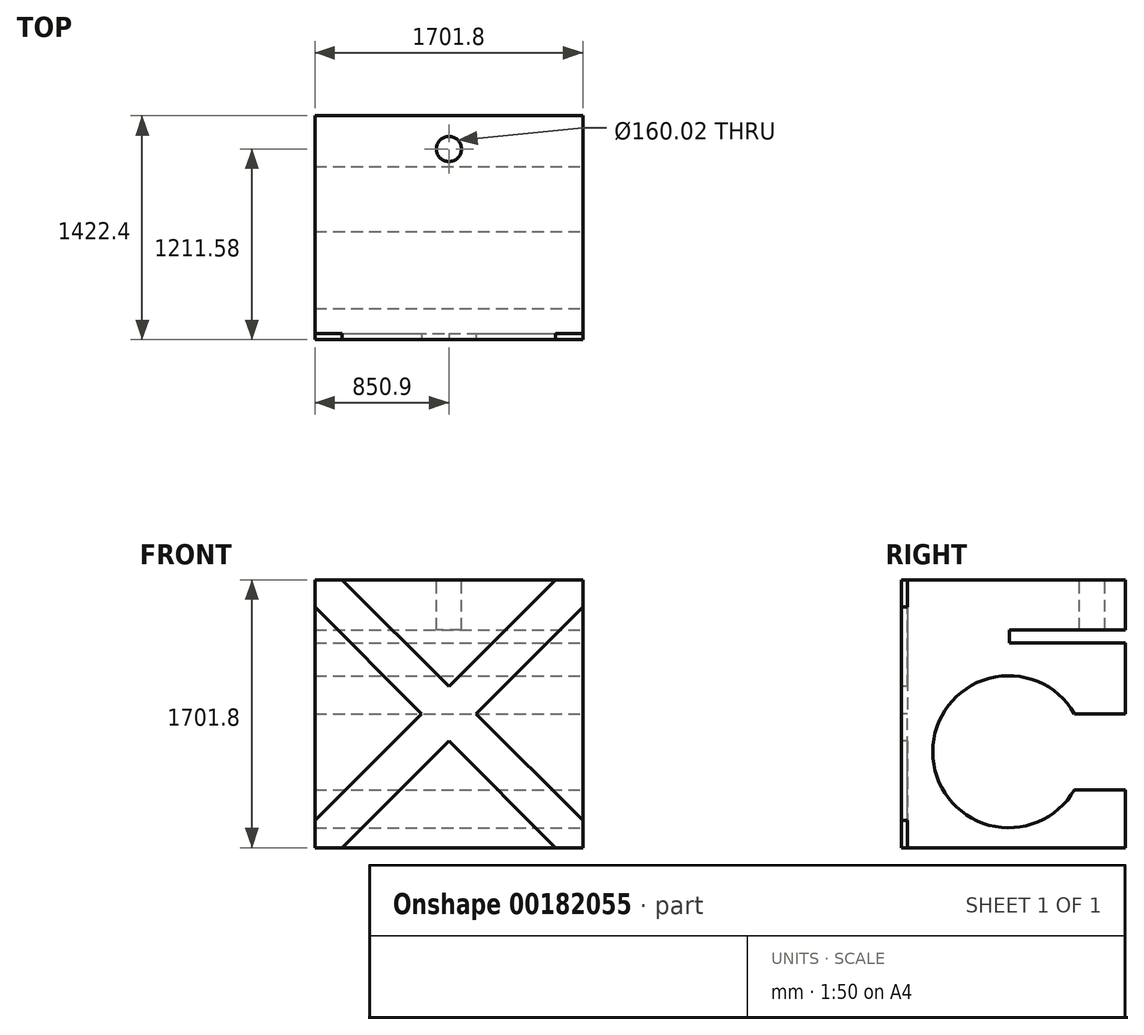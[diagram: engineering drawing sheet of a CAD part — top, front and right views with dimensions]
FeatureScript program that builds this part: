
annotation { "Feature Type Name" : "Feature", "Feature Type Description" : "" }
export const myFeature = defineFeature(function(context is Context, id is Id, definition is map)
    precondition{}
    {
        {
            var Q0;
            Q0=qCreatedBy(makeId("Front.planeOp"),FACE);
            var sketch = newSketch(context, id + "F0", { "sketchPlane" : qUnion([Q0])});
            skLineSegment(sketch, "E0.bottom", {"start": v(850.9, 850.9) * mm, "end": v(-850.9, 850.9) * mm});
            skLineSegment(sketch, "E0.top", {"start": v(850.9, -850.9) * mm, "end": v(-850.9, -850.9) * mm});
            skLineSegment(sketch, "E0.left", {"start": v(850.9, 850.9) * mm, "end": v(850.9, -850.9) * mm});
            skLineSegment(sketch, "E0.right", {"start": v(-850.9, 850.9) * mm, "end": v(-850.9, -850.9) * mm});
            skPoint(sketch, "E0.middle", {"position": v(0, 0) * mm});
            skSolve(sketch);
        }
        {
            var Q0;
            Q0 = qSketchRegion(id + "F0", true);
            extrude(context, id + "F1", {"entities" : qUnion([Q0]), "depth" : 1422.4 * mm});
        }
        {
            var Q0;
            Q0=makeQuery(id+"F1.opExtrude","CAP_FACE",FACE,{"disambiguationData":[OSD([sQuery(id+"F0.wireOp",EDGE,"E0.bottom"),sQuery(id+"F0.wireOp",EDGE,"E0.top"),sQuery(id+"F0.wireOp",EDGE,"E0.left"),sQuery(id+"F0.wireOp",EDGE,"E0.right")])],"isStart":false});
            var sketch = newSketch(context, id + "F2", { "sketchPlane" : qUnion([Q0])});
            skLineSegment(sketch, "E1", {"start": v(-980.53, -808.1) * mm, "end": v(797.03, 969.45) * mm});
            skLineSegment(sketch, "E2", {"start": v(-980.53, -808.1) * mm, "end": v(-808.1, -980.53) * mm});
            skLineSegment(sketch, "E3", {"start": v(-808.1, -980.53) * mm, "end": v(969.45, 797.03) * mm});
            skLineSegment(sketch, "E4", {"start": v(797.03, 969.45) * mm, "end": v(969.45, 797.03) * mm});
            skLineSegment(sketch, "E5", {"start": v(-1008.5, 836.08) * mm, "end": v(787.55, -959.97) * mm});
            skLineSegment(sketch, "E6", {"start": v(-836.08, 1008.5) * mm, "end": v(959.97, -787.55) * mm});
            skLineSegment(sketch, "E7", {"start": v(787.55, -959.97) * mm, "end": v(959.97, -787.55) * mm});
            skLineSegment(sketch, "E8", {"start": v(-1008.5, 836.08) * mm, "end": v(-836.08, 1008.5) * mm});
            skSolve(sketch);
        }
        {
            var Q0;
            {var subQ5=sQuery(id+"F2.wireOp",EDGE,"E5");var subQ6=sQuery(id+"F2.wireOp",EDGE,"E1");var subQ7=makeQuery(id+"F2.imprint","INTERSECT",VERTEX,{"derivedFrom":[subQ6,subQ5]});Q0=makeQuery(id+"F2.imprint","IMPRINT",FACE,{"disambiguationData":[TD([[makeQuery(id+"F2.imprint","IMPRINT",EDGE,{"disambiguationData":[TD([[subQ7,-1.0]])],"derivedFrom":subQ6}),1.0]])]});}
            var Q1;
            {var subQ5=sQuery(id+"F2.wireOp",EDGE,"E5");var subQ6=sQuery(id+"F2.wireOp",EDGE,"E1");var subQ7=makeQuery(id+"F2.imprint","INTERSECT",VERTEX,{"derivedFrom":[subQ6,subQ5]});Q1=makeQuery(id+"F2.imprint","IMPRINT",FACE,{"disambiguationData":[TD([[makeQuery(id+"F2.imprint","IMPRINT",EDGE,{"disambiguationData":[TD([[subQ7,1.0]])],"derivedFrom":subQ6}),-1.0]])]});}
            var Q2;
            {var subQ0=sQuery(id+"F2.wireOp",EDGE,"E5");var subQ1=sQuery(id+"F2.wireOp",EDGE,"E1");var subQ2=makeQuery(id+"F2.imprint","INTERSECT",VERTEX,{"derivedFrom":[subQ1,subQ0]});Q2=makeQuery(id+"F2.imprint","IMPRINT",FACE,{"disambiguationData":[TD([[makeQuery(id+"F2.imprint","IMPRINT",EDGE,{"disambiguationData":[TD([[subQ2,-1.0]])],"derivedFrom":subQ1}),-1.0]])]});}
            var Q3;
            {var subQ0=sQuery(id+"F2.wireOp",EDGE,"E6");var subQ1=sQuery(id+"F2.wireOp",EDGE,"E1");var subQ2=makeQuery(id+"F2.imprint","INTERSECT",VERTEX,{"derivedFrom":[subQ1,subQ0]});Q3=makeQuery(id+"F2.imprint","IMPRINT",FACE,{"disambiguationData":[TD([[makeQuery(id+"F2.imprint","IMPRINT",EDGE,{"disambiguationData":[TD([[subQ2,-1.0]])],"derivedFrom":subQ1}),-1.0]])]});}
            var Q4;
            {var subQ3=sQuery(id+"F2.wireOp",EDGE,"E5");var subQ6=sQuery(id+"F2.wireOp",EDGE,"E3");var subQ9=makeQuery(id+"F2.imprint","INTERSECT",VERTEX,{"derivedFrom":[subQ6,subQ3]});Q4=makeQuery(id+"F2.imprint","IMPRINT",FACE,{"disambiguationData":[TD([[makeQuery(id+"F2.imprint","IMPRINT",EDGE,{"disambiguationData":[TD([[subQ9,-1.0]])],"derivedFrom":subQ6}),-1.0]])]});}
            var Q5;
            Q5=sQuery(id+"F2.wireOp",EDGE,"E2");
            var Q6;
            Q6=sQuery(id+"F2.wireOp",EDGE,"E3");
            var Q7;
            Q7=sQuery(id+"F2.wireOp",EDGE,"E4");
            var Q8;
            Q8=sQuery(id+"F2.wireOp",EDGE,"E1");
            var Q9;
            Q9=sQuery(id+"F2.wireOp",EDGE,"E5");
            var Q10;
            Q10=sQuery(id+"F2.wireOp",EDGE,"E7");
            var Q11;
            Q11=sQuery(id+"F2.wireOp",EDGE,"E8");
            var Q12;
            Q12=sQuery(id+"F2.wireOp",EDGE,"E6");
            extrude(context, id + "F3", {"entities" : qUnion([Q0, Q1, Q2, Q3, Q4]), "operationType" : NewBodyOperationType.REMOVE, "surfaceEntities" : qUnion([Q5, Q6, Q7, Q8, Q9, Q10, Q11, Q12]), "oppositeDirection" : true, "depth" : 38.1 * mm});
        }
        {
            var Q0;
            Q0=makeQuery(id+"F1.opExtrude","SWEPT_FACE",FACE,{"disambiguationData":[OSD([sQuery(id+"F0.wireOp",EDGE,"E0.left")])]});
            var sketch = newSketch(context, id + "F4", { "sketchPlane" : qUnion([Q0])});
            skLineSegment(sketch, "E9", {"start": v(0, 533.4) * mm, "end": v(-736.6, 533.4) * mm});
            skLineSegment(sketch, "E10", {"start": v(-736.6, 533.4) * mm, "end": v(-736.6, 449.58) * mm});
            skLineSegment(sketch, "E11", {"start": v(-736.6, 449.58) * mm, "end": v(0, 449.58) * mm});
            skLineSegment(sketch, "E12", {"start": v(0, 533.4) * mm, "end": v(0, 449.58) * mm});
            skSolve(sketch);
        }
        {
            var Q0;
            Q0 = qSketchRegion(id + "F4", true);
            extrude(context, id + "F5", {"entities" : qUnion([Q0]), "operationType" : NewBodyOperationType.REMOVE, "oppositeDirection" : true, "depth" : 1950.72 * mm});
        }
        {
            var Q0;
            Q0=makeQuery(id+"F1.opExtrude","SWEPT_FACE",FACE,{"disambiguationData":[OSD([sQuery(id+"F0.wireOp",EDGE,"E0.left")])]});
            var sketch = newSketch(context, id + "F6", { "sketchPlane" : qUnion([Q0])});
            skCircle(sketch, "E13", {"center": v(-740.72, -241.3) * mm, "radius": 482.6 * mm});
            skLineSegment(sketch, "E14", {"start": v(-740.72, -241.3) * mm, "end": v(-740.72, 0) * mm});
            skLineSegment(sketch, "E15", {"start": v(-740.72, -241.3) * mm, "end": v(-740.72, -482.6) * mm});
            skLineSegment(sketch, "E16", {"start": v(-740.72, -482.6) * mm, "end": v(76.7, -482.6) * mm});
            skLineSegment(sketch, "E17", {"start": v(-740.72, 0) * mm, "end": v(76.7, 0) * mm});
            skLineSegment(sketch, "E18", {"start": v(76.7, 0) * mm, "end": v(76.7, -482.6) * mm});
            skSolve(sketch);
        }
        {
            var Q0;
            Q0 = qSketchRegion(id + "F6", true);
            extrude(context, id + "F7", {"entities" : qUnion([Q0]), "operationType" : NewBodyOperationType.REMOVE, "oppositeDirection" : true, "depth" : 2123.44 * mm});
        }
        {
            var Q0;
            Q0=makeQuery(id+"F1.opExtrude","SWEPT_FACE",FACE,{"disambiguationData":[OSD([sQuery(id+"F0.wireOp",EDGE,"E0.bottom")])]});
            var sketch = newSketch(context, id + "F8", { "sketchPlane" : qUnion([Q0])});
            skLineSegment(sketch, "E19", {"start": v(-850.9, 0) * mm, "end": v(0, 0) * mm});
            skLineSegment(sketch, "E20", {"start": v(0, 0) * mm, "end": v(0, -210.82) * mm});
            skCircle(sketch, "E21", {"center": v(0, -210.82) * mm, "radius": 80.01 * mm});
            skSolve(sketch);
        }
        {
            var Q0;
            Q0 = qSketchRegion(id + "F8", true);
            extrude(context, id + "F9", {"entities" : qUnion([Q0]), "operationType" : NewBodyOperationType.REMOVE, "oppositeDirection" : true, "depth" : 383.54 * mm});
        }
    });
